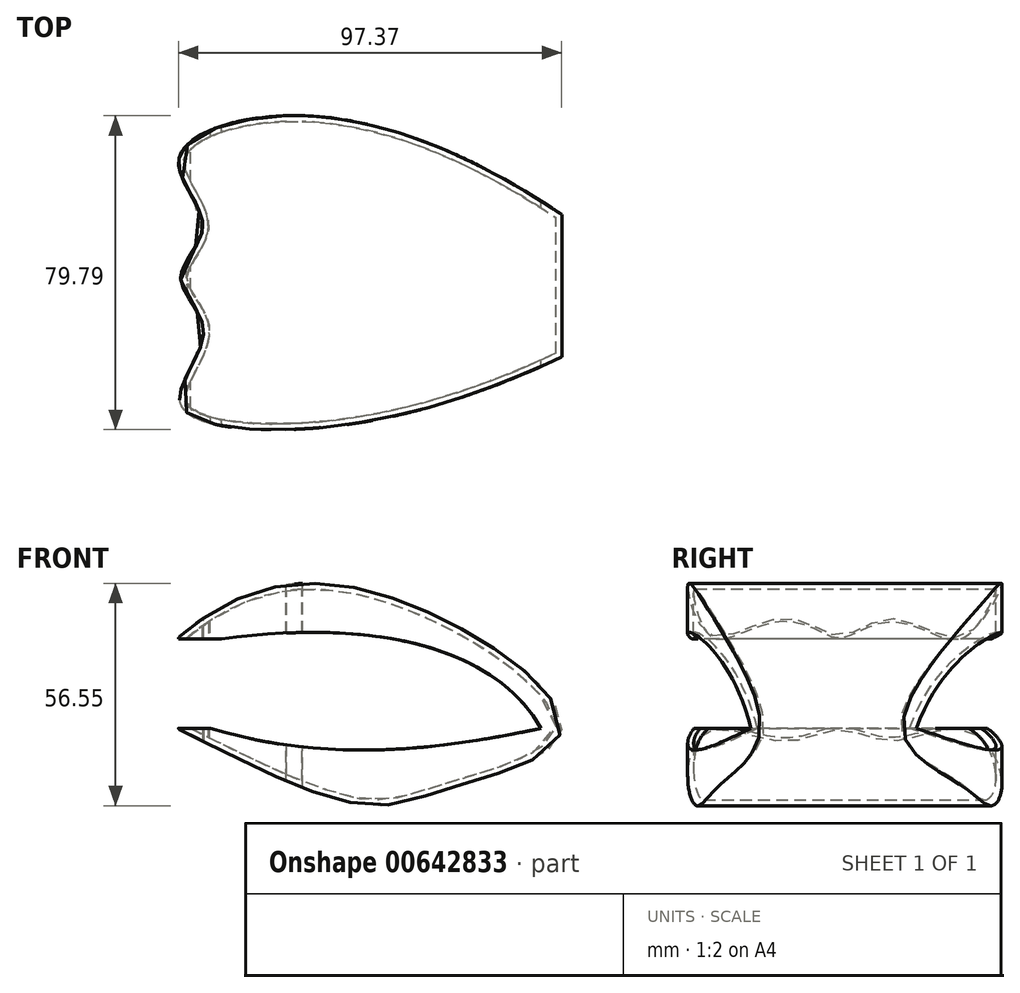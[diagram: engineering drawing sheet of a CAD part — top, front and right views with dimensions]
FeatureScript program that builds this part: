
annotation { "Feature Type Name" : "Feature", "Feature Type Description" : "" }
export const myFeature = defineFeature(function(context is Context, id is Id, definition is map)
    precondition{}
    {
        {
            var Q0;
            Q0=qCreatedBy(makeId("Front.planeOp"),FACE);
            var sketch = newSketch(context, id + "F0", { "sketchPlane" : qUnion([Q0])});
            skFitSpline(sketch, "E0", {"points": [v(-47.27, 0) * mm, v(0, -19.48) * mm, v(21.7, -15.29) * mm, v(50.3, 0) * mm, v(0, 35.23) * mm, v(-47.5, 22.73) * mm], "startDerivative": vector(240.84, -122.09) * mm, "endDerivative": vector(-178.34, -155.04) * mm});
            skLineSegment(sketch, "E1", {"start": v(-47.5, 22.73) * mm, "end": v(-36.14, 22.73) * mm});
            skFitSpline(sketch, "E2", {"points": [v(-36.14, 22.73) * mm, v(45.12, 0) * mm], "startDerivative": vector(207.95, 27.27) * mm, "endDerivative": vector(2.68, 0) * mm});
            skFitSpline(sketch, "E3", {"points": [v(45.12, 0) * mm, v(-38.86, 0) * mm], "startDerivative": vector(-77.67, -16.27) * mm, "endDerivative": vector(-90.24, 27.37) * mm});
            skLineSegment(sketch, "E4", {"start": v(-38.86, 0) * mm, "end": v(-47.27, 0) * mm});
            skSolve(sketch);
        }
        {
            var Q0;
            Q0 = qSketchRegion(id + "F0", true);
            extrude(context, id + "F1", {"entities" : qUnion([Q0]), "depth" : 80 * mm, "offsetDistance" : 25.4 * mm});
        }
        {
            var Q0;
            Q0=qCreatedBy(makeId("Top.planeOp"),FACE);
            var sketch = newSketch(context, id + "F2", { "sketchPlane" : qUnion([Q0])});
            skFitSpline(sketch, "E5", {"points": [v(54.74, -28.18) * mm, v(-19.65, 0) * mm, v(-47.01, -11.44) * mm, v(-40.88, -28.08) * mm, v(-46.48, -41.2) * mm, v(-40.64, -54.75) * mm, v(-46.75, -72.55) * mm, v(-18.59, -79.72) * mm, v(55, -59) * mm], "startDerivative": vector(-390.54, 276.57) * mm, "endDerivative": vector(405.63, 202.95) * mm});
            skLineSegment(sketch, "E6", {"start": v(54.74, -28.18) * mm, "end": v(54.74, 28.41) * mm});
            skLineSegment(sketch, "E7", {"start": v(54.74, 28.41) * mm, "end": v(-72.25, 20.97) * mm});
            skLineSegment(sketch, "E8", {"start": v(-72.25, 20.97) * mm, "end": v(-69.33, -97.52) * mm});
            skLineSegment(sketch, "E9", {"start": v(-69.33, -97.52) * mm, "end": v(47.55, -94.64) * mm});
            skLineSegment(sketch, "E10", {"start": v(47.55, -94.64) * mm, "end": v(62.71, -81.58) * mm});
            skLineSegment(sketch, "E11", {"start": v(62.71, -81.58) * mm, "end": v(55, -59) * mm});
            skSolve(sketch);
        }
        {
            var Q0;
            Q0 = qSketchRegion(id + "F2", true);
            extrude(context, id + "F3", {"entities" : qUnion([Q0]), "operationType" : NewBodyOperationType.REMOVE, "endBound" : BoundingType.SYMMETRIC, "oppositeDirection" : true, "depth" : 100 * mm, "offsetDistance" : 25 * mm});
        }
        {
            var Q0;
            Q0=makeQuery(id+"F1.opExtrude","SWEPT_FACE",FACE,{"disambiguationData":[OSD([sQuery(id+"F0.wireOp",EDGE,"E3")])]});
            var Q1;
            Q1=makeQuery(id+"F1.opExtrude","SWEPT_FACE",FACE,{"disambiguationData":[OSD([sQuery(id+"F0.wireOp",EDGE,"E2")])]});
            var Q2;
            Q2=makeQuery(id+"F1.opExtrude","SWEPT_FACE",FACE,{"disambiguationData":[OSD([sQuery(id+"F0.wireOp",EDGE,"E1")])]});
            var Q3;
            Q3=makeQuery(id+"F1.opExtrude","SWEPT_FACE",FACE,{"disambiguationData":[OSD([sQuery(id+"F0.wireOp",EDGE,"E4")])]});
            shell(context, id + "F4", {"entities" : qUnion([Q0, Q1, Q2, Q3]), "thickness" : 1.5 * mm});
        }
    });
